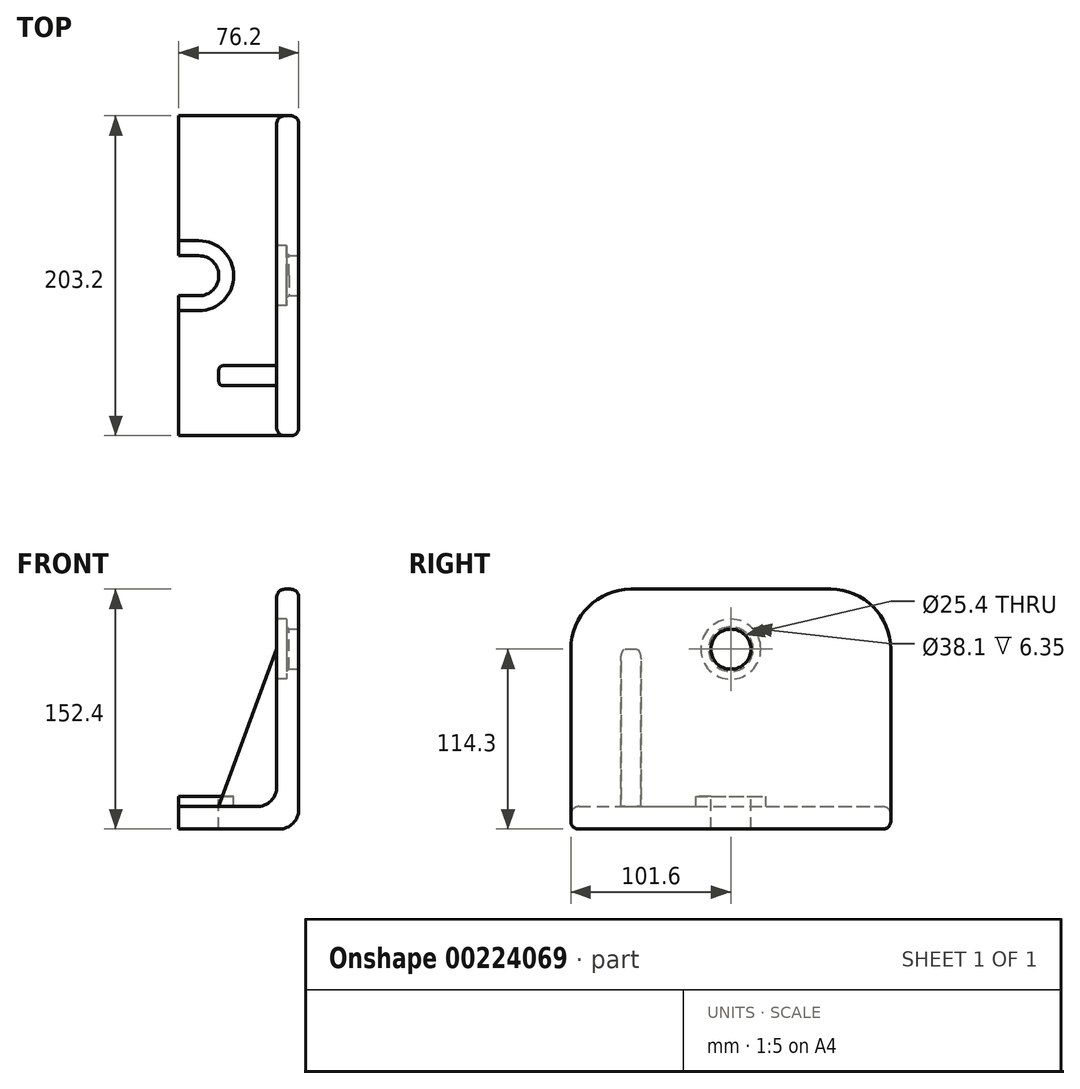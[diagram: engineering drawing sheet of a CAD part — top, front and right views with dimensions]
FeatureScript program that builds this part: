
annotation { "Feature Type Name" : "Feature", "Feature Type Description" : "" }
export const myFeature = defineFeature(function(context is Context, id is Id, definition is map)
    precondition{}
    {
        {
            var Q0;
            Q0=qCreatedBy(makeId("Front.planeOp"),FACE);
            var sketch = newSketch(context, id + "F0", { "sketchPlane" : qUnion([Q0])});
            skLineSegment(sketch, "E0", {"start": v(0, 0) * mm, "end": v(-76.2, 0) * mm});
            skLineSegment(sketch, "E1", {"start": v(-76.2, 0) * mm, "end": v(-76.2, 14.31) * mm});
            skLineSegment(sketch, "E2", {"start": v(-76.2, 14.31) * mm, "end": v(-14, 14.31) * mm});
            skLineSegment(sketch, "E3", {"start": v(-14, 14.31) * mm, "end": v(-14, 152.4) * mm});
            skLineSegment(sketch, "E4", {"start": v(-14, 152.4) * mm, "end": v(0, 152.4) * mm});
            skLineSegment(sketch, "E5", {"start": v(0, 152.4) * mm, "end": v(0, 0) * mm});
            skSolve(sketch);
        }
        {
            var Q0;
            Q0 = qSketchRegion(id + "F0", true);
            extrude(context, id + "F1", {"entities" : qUnion([Q0]), "endBound" : BoundingType.SYMMETRIC, "depth" : 203.2 * mm});
        }
        {
            var Q0;
            Q0=makeQuery(id+"F1.opExtrude","SWEPT_FACE",FACE,{"disambiguationData":[OSD([sQuery(id+"F0.wireOp",EDGE,"E5")])]});
            var sketch = newSketch(context, id + "F2", { "sketchPlane" : qUnion([Q0])});
            skCircle(sketch, "E6", {"center": v(0, 114.3) * mm, "radius": 12.7 * mm});
            skSolve(sketch);
        }
        {
            var Q0;
            Q0=makeQuery(id+"F2.imprint","IMPRINT",FACE,{"disambiguationData":[TD([[makeQuery(id+"F2.imprint","IMPRINT",EDGE,{"derivedFrom":sQuery(id+"F2.wireOp",EDGE,"E6")}),1.0]])]});
            extrude(context, id + "F3", {"entities" : qUnion([Q0]), "operationType" : NewBodyOperationType.REMOVE, "endBound" : BoundingType.THROUGH_ALL, "oppositeDirection" : true, "depth" : 25.4 * mm});
        }
        {
            var Q0;
            Q0=makeQuery(id+"F1.opExtrude","SWEPT_FACE",FACE,{"disambiguationData":[OSD([sQuery(id+"F0.wireOp",EDGE,"E2")])]});
            var sketch = newSketch(context, id + "F4", { "sketchPlane" : qUnion([Q0])});
            skArc(sketch, "E7", {"start": v(-63.5, -12.7) * mm, "mid": v(-50.8, 0) * mm, "end": v(-63.5, 12.7) * mm});
            skLineSegment(sketch, "E8", {"start": v(-63.5, -12.7) * mm, "end": v(-76.2, -12.7) * mm});
            skLineSegment(sketch, "E9", {"start": v(-63.5, 12.7) * mm, "end": v(-76.2, 12.7) * mm});
            skLineSegment(sketch, "E10", {"start": v(-76.2, 12.7) * mm, "end": v(-76.2, -12.7) * mm});
            skSolve(sketch);
        }
        {
            var Q0;
            Q0=makeQuery(id+"F4.imprint","IMPRINT",FACE,{"disambiguationData":[TD([[makeQuery(id+"F4.imprint","IMPRINT",EDGE,{"derivedFrom":sQuery(id+"F4.wireOp",EDGE,"E7")}),1.0]])]});
            extrude(context, id + "F5", {"entities" : qUnion([Q0]), "operationType" : NewBodyOperationType.REMOVE, "endBound" : BoundingType.THROUGH_ALL, "oppositeDirection" : true, "depth" : 25.4 * mm});
        }
        {
            var Q0;
            Q0=makeQuery(id+"F1.opExtrude","CAP_EDGE",EDGE,{"disambiguationData":[OSD([sQuery(id+"F0.wireOp",EDGE,"E4")])],"isStart":false});
            var Q1;
            Q1=makeQuery(id+"F1.opExtrude","CAP_EDGE",EDGE,{"disambiguationData":[OSD([sQuery(id+"F0.wireOp",EDGE,"E4")])],"isStart":true});
            fillet(context, id + "F6", {"entities" : qUnion([Q0, Q1]), "radius" : 38.1 * mm, "tangentPropagation" : true, "allowEdgeOverflow" : false});
        }
        {
            var Q0;
            Q0=makeQuery(id+"F1.opExtrude","SWEPT_FACE",FACE,{"disambiguationData":[OSD([sQuery(id+"F0.wireOp",EDGE,"E3")])]});
            var sketch = newSketch(context, id + "F7", { "sketchPlane" : qUnion([Q0])});
            skCircle(sketch, "E11", {"center": v(0, 114.3) * mm, "radius": 19.05 * mm});
            skSolve(sketch);
        }
        {
            var Q0;
            Q0 = qSketchRegion(id + "F7", true);
            extrude(context, id + "F8", {"entities" : qUnion([Q0]), "operationType" : NewBodyOperationType.REMOVE, "oppositeDirection" : true, "depth" : 6.35 * mm});
        }
        {
            var Q0;
            Q0=qCreatedBy(makeId("Front.planeOp"),FACE);
            cPlane(context, id + "F9", {"entities" : qUnion([Q0]), "cplaneType" : CPlaneType.OFFSET, "offset" : 63.5 * mm, "width" : 152.4 * mm, "height" : 152.4 * mm});
        }
        {
            var Q0;
            Q0=qCreatedBy(id+"F9.planeOp",FACE);
            var sketch = newSketch(context, id + "F10", { "sketchPlane" : qUnion([Q0])});
            skLineSegment(sketch, "E12.0", {"start": v(-50.8, 14.31) * mm, "end": v(-14, 14.31) * mm});
            skLineSegment(sketch, "E13.0", {"start": v(-14, 14.31) * mm, "end": v(-14, 114.3) * mm});
            skLineSegment(sketch, "E14", {"start": v(-14, 114.3) * mm, "end": v(-50.8, 14.31) * mm});
            skPoint(sketch, "E15.orphan", {"position": v(-76.2, 14.31) * mm});
            skSolve(sketch);
        }
        {
            var Q0;
            Q0=makeQuery(id+"F10.imprint","IMPRINT",FACE,{"disambiguationData":[TD([[makeQuery(id+"F10.imprint","IMPRINT",EDGE,{"derivedFrom":sQuery(id+"F10.wireOp",EDGE,"E12.0")}),1.0]])]});
            extrude(context, id + "F11", {"entities" : qUnion([Q0]), "operationType" : NewBodyOperationType.ADD, "endBound" : BoundingType.SYMMETRIC, "depth" : 12.7 * mm});
        }
        {
            var Q0;
            Q0=makeQuery(id+"F8.boolean.opBoolean","COPY",EDGE,{"derivedFrom":makeQuery(id+"F8.opExtrude","CAP_EDGE",EDGE,{"disambiguationData":[OSD([sQuery(id+"F7.wireOp",EDGE,"E11")])],"isStart":true})});
            var Q1;
            Q1=makeQuery(id+"F8.boolean.opBoolean","INTERSECT",EDGE,{"derivedFrom":[makeQuery(id+"F3.boolean.opBoolean","COPY",FACE,{"derivedFrom":makeQuery(id+"F3.opExtrude","SWEPT_FACE",FACE,{"disambiguationData":[OSD([sQuery(id+"F2.wireOp",EDGE,"E6")])]})}),makeQuery(id+"F8.opExtrude","CAP_FACE",FACE,{"disambiguationData":[OSD([sQuery(id+"F7.wireOp",EDGE,"E11")])],"isStart":false})]});
            chamfer(context, id + "F12", {"entities" : qUnion([Q0, Q1]), "width" : 1.52 * mm, "tangentPropagation" : true});
        }
        {
            var Q0;
            {var subQ2=sQuery(id+"F0.wireOp",EDGE,"E1");Q0=makeQuery(id+"F5.boolean.opBoolean","SPLIT",FACE,{"disambiguationData":[TD([makeQuery(id+"F5.opExtrude","SWEPT_FACE",FACE,{"disambiguationData":[OSD([sQuery(id+"F4.wireOp",EDGE,"E8")])]})])],"derivedFrom":makeQuery(id+"F1.opExtrude","SWEPT_FACE",FACE,{"disambiguationData":[OSD([subQ2])]})});}
            var sketch = newSketch(context, id + "F13", { "sketchPlane" : qUnion([Q0])});
            skLineSegment(sketch, "E16.bottom", {"start": v(12.7, 14.31) * mm, "end": v(22.23, 14.31) * mm});
            skLineSegment(sketch, "E16.top", {"start": v(12.7, 20.66) * mm, "end": v(22.23, 20.66) * mm});
            skLineSegment(sketch, "E16.left", {"start": v(12.7, 14.31) * mm, "end": v(12.7, 20.66) * mm});
            skLineSegment(sketch, "E16.right", {"start": v(22.23, 14.31) * mm, "end": v(22.23, 20.66) * mm});
            skSolve(sketch);
        }
        {
            var Q0;
            Q0=makeQuery(id+"F1.opExtrude","SWEPT_FACE",FACE,{"disambiguationData":[OSD([sQuery(id+"F0.wireOp",EDGE,"E2")])]});
            var sketch = newSketch(context, id + "F14", { "sketchPlane" : qUnion([Q0])});
            skArc(sketch, "E17.0", {"start": v(-63.5, -12.7) * mm, "mid": v(-50.8, 0) * mm, "end": v(-63.5, 12.7) * mm});
            skLineSegment(sketch, "E18.0", {"start": v(-63.5, 12.7) * mm, "end": v(-76.2, 12.7) * mm});
            skLineSegment(sketch, "E19.0", {"start": v(-63.5, -12.7) * mm, "end": v(-76.2, -12.7) * mm});
            skSolve(sketch);
        }
        {
            var Q0;
            Q0=makeQuery(id+"F13.imprint","IMPRINT",FACE,{"disambiguationData":[TD([[makeQuery(id+"F13.imprint","IMPRINT",EDGE,{"derivedFrom":sQuery(id+"F13.wireOp",EDGE,"E16.bottom")}),-1.0]])]});
            var Q1;
            Q1=sQuery(id+"F14.wireOp",EDGE,"E19.0");
            var Q2;
            Q2=sQuery(id+"F14.wireOp",EDGE,"E17.0");
            var Q3;
            Q3=sQuery(id+"F14.wireOp",EDGE,"E18.0");
            sweep(context, id + "F15", {"operationType" : NewBodyOperationType.ADD, "profiles" : qUnion([Q0]), "path" : qUnion([Q1, Q2, Q3])});
        }
        {
            var Q0;
            {var subQ0=sQuery(id+"F0.wireOp",EDGE,"E3");var subQ1=sQuery(id+"F0.wireOp",EDGE,"E2");Q0=makeQuery(id+"F11.boolean.opBoolean","SPLIT",EDGE,{"disambiguationData":[TD([makeQuery(id+"F11.opExtrude","CAP_FACE",FACE,{"disambiguationData":[OSD([sQuery(id+"F10.wireOp",EDGE,"E12.0"),sQuery(id+"F10.wireOp",EDGE,"E13.0"),sQuery(id+"F10.wireOp",EDGE,"E14")])],"isStart":false})])],"derivedFrom":makeQuery(id+"F1.opExtrude","SWEPT_EDGE",EDGE,{"disambiguationData":[OSD([subQ1,subQ0])]})});}
            var Q1;
            {var subQ0=sQuery(id+"F0.wireOp",EDGE,"E2");var subQ2=sQuery(id+"F0.wireOp",EDGE,"E3");var subQ4=sQuery(id+"F10.wireOp",EDGE,"E14");var subQ5=sQuery(id+"F10.wireOp",EDGE,"E13.0");var subQ6=sQuery(id+"F10.wireOp",EDGE,"E12.0");var subQ7=makeQuery(id+"F11.opExtrude","CAP_FACE",FACE,{"disambiguationData":[OSD([subQ6,subQ5,subQ4])],"isStart":true});Q1=makeQuery(id+"F9W6PPdVI64KEGn_1.1.F11.boolean.opBoolean","SPLIT",EDGE,{"disambiguationData":[TD([subQ7])],"derivedFrom":makeQuery(id+"F11.boolean.opBoolean","SPLIT",EDGE,{"disambiguationData":[TD([subQ7])],"derivedFrom":makeQuery(id+"F1.opExtrude","SWEPT_EDGE",EDGE,{"disambiguationData":[OSD([subQ0,subQ2])]})})});}
            var Q2;
            {var subQ0=sQuery(id+"F0.wireOp",EDGE,"E3");var subQ1=sQuery(id+"F0.wireOp",EDGE,"E2");var subQ5=sQuery(id+"F10.wireOp",EDGE,"E14");var subQ6=sQuery(id+"F10.wireOp",EDGE,"E13.0");var subQ7=sQuery(id+"F10.wireOp",EDGE,"E12.0");Q2=makeQuery(id+"F9W6PPdVI64KEGn_1.1.F11.boolean.opBoolean","SPLIT",EDGE,{"disambiguationData":[TD([makeQuery(id+"F9W6PPdVI64KEGn_1.1.F11.opExtrude","CAP_FACE",FACE,{"disambiguationData":[OSD([subQ7,subQ6,subQ5])],"isStart":false})])],"derivedFrom":makeQuery(id+"F11.boolean.opBoolean","SPLIT",EDGE,{"disambiguationData":[TD([makeQuery(id+"F11.opExtrude","CAP_FACE",FACE,{"disambiguationData":[OSD([subQ7,subQ6,subQ5])],"isStart":true})])],"derivedFrom":makeQuery(id+"F1.opExtrude","SWEPT_EDGE",EDGE,{"disambiguationData":[OSD([subQ1,subQ0])]})})});}
            fillet(context, id + "F16", {"entities" : qUnion([Q0, Q1, Q2]), "radius" : 12.7 * mm, "tangentPropagation" : true, "allowEdgeOverflow" : false});
        }
        {
            var Q0;
            Q0=makeQuery(id+"F1.opExtrude","SWEPT_EDGE",EDGE,{"disambiguationData":[OSD([sQuery(id+"F0.wireOp",EDGE,"E0"),sQuery(id+"F0.wireOp",EDGE,"E5")])]});
            fillet(context, id + "F17", {"entities" : qUnion([Q0]), "radius" : 12.7 * mm, "tangentPropagation" : true, "allowEdgeOverflow" : false});
        }
        {
            var Q0;
            Q0=makeQuery(id+"F1.opExtrude","CAP_EDGE",EDGE,{"disambiguationData":[OSD([sQuery(id+"F0.wireOp",EDGE,"E2")])],"isStart":false});
            var Q1;
            Q1=makeQuery(id+"F6.opFillet","BLEND_EDGE",EDGE,{"blendedFrom":[makeQuery(id+"F1.opExtrude","CAP_EDGE",EDGE,{"disambiguationData":[OSD([sQuery(id+"F0.wireOp",EDGE,"E4")])],"isStart":false}),makeQuery(id+"F1.opExtrude","SWEPT_FACE",FACE,{"disambiguationData":[OSD([sQuery(id+"F0.wireOp",EDGE,"E5")])]})],"blendedInto":[makeQuery(id+"F1.opExtrude","SWEPT_FACE",FACE,{"disambiguationData":[OSD([sQuery(id+"F0.wireOp",EDGE,"E5")])]})]});
            fillet(context, id + "F18", {"entities" : qUnion([Q0, Q1]), "radius" : 5.08 * mm, "tangentPropagation" : true, "allowEdgeOverflow" : false});
        }
        {
            var Q0;
            Q0=makeQuery(id+"F9W6PPdVI64KEGn_1.1.F11.opExtrude","CAP_EDGE",EDGE,{"disambiguationData":[OSD([sQuery(id+"F10.wireOp",EDGE,"E14")])],"isStart":true});
            var Q1;
            Q1=makeQuery(id+"F9W6PPdVI64KEGn_1.1.F11.opExtrude","CAP_EDGE",EDGE,{"disambiguationData":[OSD([sQuery(id+"F10.wireOp",EDGE,"E14")])],"isStart":false});
            var Q2;
            Q2=makeQuery(id+"F11.opExtrude","CAP_EDGE",EDGE,{"disambiguationData":[OSD([sQuery(id+"F10.wireOp",EDGE,"E14")])],"isStart":false});
            var Q3;
            Q3=makeQuery(id+"F11.opExtrude","CAP_EDGE",EDGE,{"disambiguationData":[OSD([sQuery(id+"F10.wireOp",EDGE,"E14")])],"isStart":true});
            var Q4;
            Q4=makeQuery(id+"F9W6PPdVI64KEGn_1.1.F11.opExtrude","CAP_EDGE",EDGE,{"disambiguationData":[OSD([sQuery(id+"F10.wireOp",EDGE,"E13.0")])],"isStart":true});
            var Q5;
            Q5=makeQuery(id+"F11.opExtrude","CAP_EDGE",EDGE,{"disambiguationData":[OSD([sQuery(id+"F10.wireOp",EDGE,"E13.0")])],"isStart":false});
            var Q6;
            Q6=makeQuery(id+"F15.opSweep","SWEPT_EDGE",EDGE,{"disambiguationData":[OSD([sQuery(id+"F0.wireOp",EDGE,"E1"),sQuery(id+"F0.wireOp",EDGE,"E2"),sQuery(id+"F13.wireOp",EDGE,"E16.bottom"),sQuery(id+"F13.wireOp",EDGE,"E16.right"),sQuery(id+"F14.wireOp",EDGE,"E19.0")])]});
            fillet(context, id + "F19", {"entities" : qUnion([Q0, Q1, Q2, Q3, Q4, Q5, Q6]), "radius" : 2.54 * mm, "tangentPropagation" : true, "allowEdgeOverflow" : false});
        }
    });
